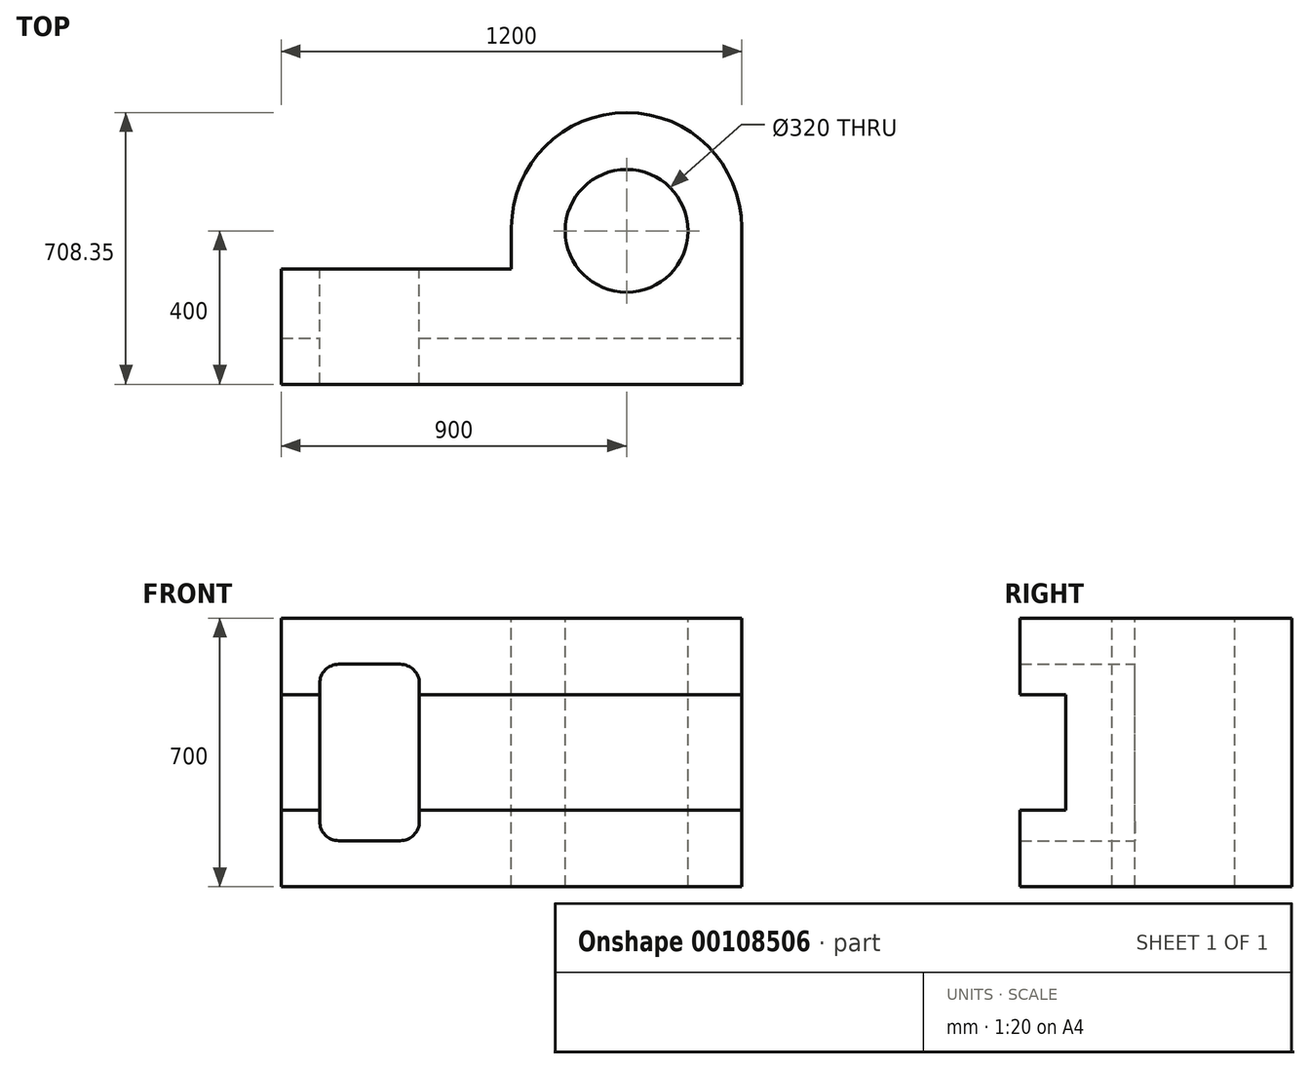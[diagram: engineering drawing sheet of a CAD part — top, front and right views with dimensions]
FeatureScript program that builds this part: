
annotation { "Feature Type Name" : "Feature", "Feature Type Description" : "" }
export const myFeature = defineFeature(function(context is Context, id is Id, definition is map)
    precondition{}
    {
        {
            var Q0;
            Q0=qCreatedBy(makeId("Front.planeOp"),FACE);
            var sketch = newSketch(context, id + "F0", { "sketchPlane" : qUnion([Q0])});
            skLineSegment(sketch, "E0.bottom", {"start": v(600, -350) * mm, "end": v(-600, -350) * mm});
            skLineSegment(sketch, "E0.top", {"start": v(600, 350) * mm, "end": v(-600, 350) * mm});
            skLineSegment(sketch, "E0.left", {"start": v(600, -350) * mm, "end": v(600, 350) * mm});
            skLineSegment(sketch, "E0.right", {"start": v(-600, -350) * mm, "end": v(-600, 350) * mm});
            skPoint(sketch, "E0.middle", {"position": v(0, 0) * mm});
            skSolve(sketch);
        }
        {
            var Q0;
            Q0=makeQuery(id+"F0.imprint","IMPRINT",FACE,{"disambiguationData":[TD([[makeQuery(id+"F0.imprint","IMPRINT",EDGE,{"derivedFrom":sQuery(id+"F0.wireOp",EDGE,"E0.bottom")}),-1.0]])]});
            extrude(context, id + "F1", {"entities" : qUnion([Q0]), "depth" : 300 * mm});
        }
        {
            var Q0;
            Q0=makeQuery(id+"F1.opExtrude","SWEPT_FACE",FACE,{"disambiguationData":[OSD([sQuery(id+"F0.wireOp",EDGE,"E0.top")])]});
            var sketch = newSketch(context, id + "F2", { "sketchPlane" : qUnion([Q0])});
            skPoint(sketch, "E1.oppositeSnap0", {"position": v(600, -150) * mm});
            skLineSegment(sketch, "E2", {"start": v(-600, -300) * mm, "end": v(195, -300) * mm});
            skPoint(sketch, "E1.top.end.orphan", {"position": v(600, 196.32) * mm});
            skLineSegment(sketch, "E3", {"start": v(0, 0) * mm, "end": v(0, 108.35) * mm});
            skLineSegment(sketch, "E4", {"start": v(600, 108.35) * mm, "end": v(600, 0) * mm});
            skLineSegment(sketch, "E5", {"start": v(600, 0) * mm, "end": v(0, 0) * mm});
            skArc(sketch, "E6", {"start": v(600, 108.35) * mm, "mid": v(300, 408.35) * mm, "end": v(0, 108.35) * mm});
            skSolve(sketch);
        }
        {
            var Q0;
            Q0 = qSketchRegion(id + "F2", true);
            extrude(context, id + "F3", {"entities" : qUnion([Q0]), "operationType" : NewBodyOperationType.ADD, "oppositeDirection" : true, "depth" : 700 * mm});
        }
        {
            var Q0;
            {var subQ0=sQuery(id+"F2.wireOp",EDGE,"E4");Q0=makeQuery(id+"FSXr5VxJJuYyIoz_2.boolean.opBoolean","MERGE",FACE,{"derivedFrom":[makeQuery(id+"F1.opExtrude","SWEPT_FACE",FACE,{"disambiguationData":[OSD([sQuery(id+"F0.wireOp",EDGE,"E0.left")])]}),makeQuery(id+"FvFI1RLhSDKojJz_1.opExtrude","SWEPT_FACE",FACE,{"disambiguationData":[OSD([subQ0])]}),makeQuery(id+"FSXr5VxJJuYyIoz_2.opExtrude","SWEPT_FACE",FACE,{"disambiguationData":[OSD([subQ0])]})]});}
            var sketch = newSketch(context, id + "F4", { "sketchPlane" : qUnion([Q0])});
            skSolve(sketch);
        }
        {
            var Q0;
            {var subQ0=sQuery(id+"F0.wireOp",EDGE,"E0.left");Q0=makeQuery(id+"F4.imprint","IMPRINT",FACE,{"disambiguationData":[TD([[makeQuery(id+"F4.imprint","IMPRINT",EDGE,{"derivedFrom":makeQuery(id+"F1.opExtrude","CAP_EDGE",EDGE,{"disambiguationData":[OSD([subQ0])],"isStart":false})}),-1.0]])]});}
            var sketch = newSketch(context, id + "F5", { "sketchPlane" : qUnion([Q0])});
            skPoint(sketch, "E7", {"position": v(-300, 0) * mm});
            skLineSegment(sketch, "E8.bottom", {"start": v(-420, -150) * mm, "end": v(-180, -150) * mm});
            skLineSegment(sketch, "E8.top", {"start": v(-420, 150) * mm, "end": v(-180, 150) * mm});
            skLineSegment(sketch, "E8.left", {"start": v(-420, -150) * mm, "end": v(-420, 150) * mm});
            skLineSegment(sketch, "E8.right", {"start": v(-180, -150) * mm, "end": v(-180, 150) * mm});
            skSolve(sketch);
        }
        {
            var Q0;
            Q0 = qSketchRegion(id + "F5", true);
            extrude(context, id + "F6", {"entities" : qUnion([Q0]), "operationType" : NewBodyOperationType.REMOVE, "endBound" : BoundingType.THROUGH_ALL, "oppositeDirection" : true, "depth" : 25 * mm});
        }
        {
            var Q0;
            Q0=makeQuery(id+"F1.opExtrude","CAP_FACE",FACE,{"disambiguationData":[OSD([sQuery(id+"F0.wireOp",EDGE,"E0.bottom"),sQuery(id+"F0.wireOp",EDGE,"E0.top"),sQuery(id+"F0.wireOp",EDGE,"E0.left"),sQuery(id+"F0.wireOp",EDGE,"E0.right")])],"isStart":true});
            var sketch = newSketch(context, id + "F7", { "sketchPlane" : qUnion([Q0])});
            skLineSegment(sketch, "E9.bottom", {"start": v(500, -230) * mm, "end": v(240, -230) * mm});
            skLineSegment(sketch, "E9.top", {"start": v(500, 230) * mm, "end": v(240, 230) * mm});
            skLineSegment(sketch, "E9.left", {"start": v(500, -230) * mm, "end": v(500, 230) * mm});
            skLineSegment(sketch, "E9.right", {"start": v(240, -230) * mm, "end": v(240, 230) * mm});
            skPoint(sketch, "E9.middle", {"position": v(370, 0) * mm});
            skSolve(sketch);
        }
        {
            var Q0;
            Q0 = qSketchRegion(id + "F7", true);
            extrude(context, id + "F8", {"entities" : qUnion([Q0]), "operationType" : NewBodyOperationType.REMOVE, "endBound" : BoundingType.THROUGH_ALL, "oppositeDirection" : true, "depth" : 25 * mm});
        }
        {
            var Q0;
            Q0=makeQuery(id+"F8.boolean.opBoolean","COPY",EDGE,{"derivedFrom":makeQuery(id+"F8.opExtrude","SWEPT_EDGE",EDGE,{"disambiguationData":[OSD([sQuery(id+"F7.wireOp",EDGE,"E9.bottom"),sQuery(id+"F7.wireOp",EDGE,"E9.right")])]})});
            var Q1;
            Q1=makeQuery(id+"F8.boolean.opBoolean","COPY",EDGE,{"derivedFrom":makeQuery(id+"F8.opExtrude","SWEPT_EDGE",EDGE,{"disambiguationData":[OSD([sQuery(id+"F7.wireOp",EDGE,"E9.top"),sQuery(id+"F7.wireOp",EDGE,"E9.right")])]})});
            var Q2;
            Q2=makeQuery(id+"F8.boolean.opBoolean","COPY",EDGE,{"derivedFrom":makeQuery(id+"F8.opExtrude","SWEPT_EDGE",EDGE,{"disambiguationData":[OSD([sQuery(id+"F7.wireOp",EDGE,"E9.top"),sQuery(id+"F7.wireOp",EDGE,"E9.left")])]})});
            var Q3;
            Q3=makeQuery(id+"F8.boolean.opBoolean","COPY",EDGE,{"derivedFrom":makeQuery(id+"F8.opExtrude","SWEPT_EDGE",EDGE,{"disambiguationData":[OSD([sQuery(id+"F7.wireOp",EDGE,"E9.bottom"),sQuery(id+"F7.wireOp",EDGE,"E9.left")])]})});
            fillet(context, id + "F9", {"entities" : qUnion([Q0, Q1, Q2, Q3]), "radius" : 50 * mm, "tangentPropagation" : true, "allowEdgeOverflow" : false});
        }
        {
            var Q0;
            Q0=makeQuery(id+"F3.boolean.opBoolean","MERGE",FACE,{"derivedFrom":[makeQuery(id+"F1.opExtrude","SWEPT_FACE",FACE,{"disambiguationData":[OSD([sQuery(id+"F0.wireOp",EDGE,"E0.top")])]}),makeQuery(id+"F3.opExtrude","CAP_FACE",FACE,{"disambiguationData":[OSD([sQuery(id+"F2.wireOp",EDGE,"E3"),sQuery(id+"F2.wireOp",EDGE,"E4"),sQuery(id+"F2.wireOp",EDGE,"E5"),sQuery(id+"F2.wireOp",EDGE,"E6")])],"isStart":true})]});
            var sketch = newSketch(context, id + "F10", { "sketchPlane" : qUnion([Q0])});
            skCircle(sketch, "E10", {"center": v(300, 100) * mm, "radius": 160 * mm});
            skSolve(sketch);
        }
        {
            var Q0;
            Q0 = qSketchRegion(id + "F10", true);
            extrude(context, id + "F11", {"entities" : qUnion([Q0]), "operationType" : NewBodyOperationType.REMOVE, "endBound" : BoundingType.THROUGH_ALL, "oppositeDirection" : true, "depth" : 25 * mm});
        }
    });
